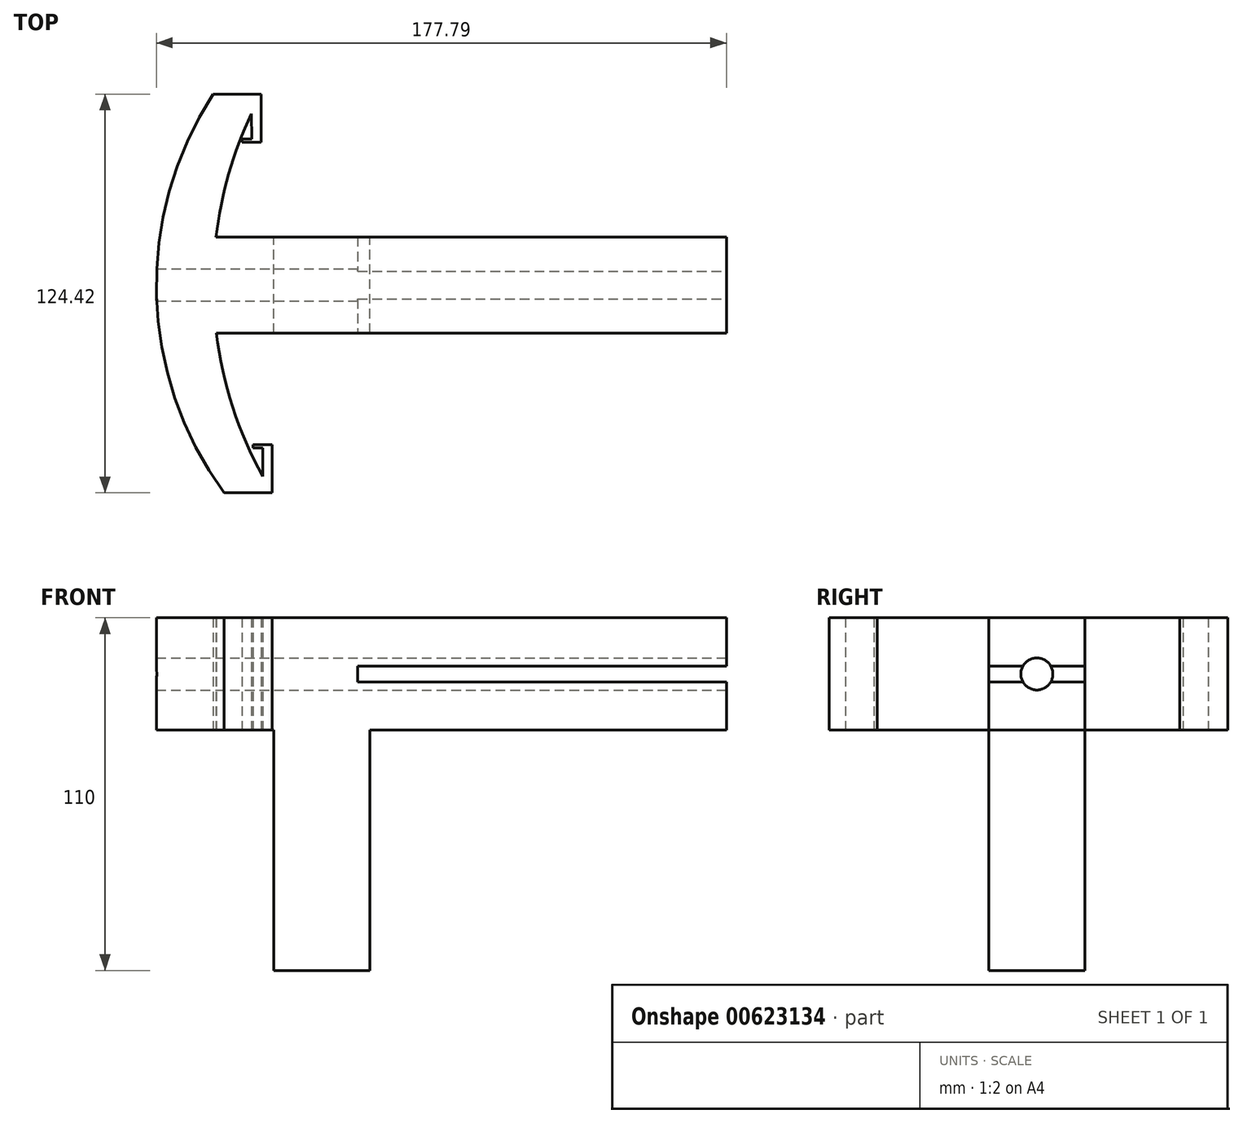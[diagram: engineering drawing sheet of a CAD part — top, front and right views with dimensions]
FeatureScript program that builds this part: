
annotation { "Feature Type Name" : "Feature", "Feature Type Description" : "" }
export const myFeature = defineFeature(function(context is Context, id is Id, definition is map)
    precondition{}
    {
        {
            var Q0;
            Q0=qCreatedBy(makeId("Top.planeOp"),FACE);
            var sketch = newSketch(context, id + "F0", { "sketchPlane" : qUnion([Q0])});
            skPoint(sketch, "E0", {"position": v(-80.73, 0) * mm});
            skArc(sketch, "E1", {"start": v(-62.98, 59.58) * mm, "mid": v(-80.7, -3.16) * mm, "end": v(-59.59, -64.84) * mm});
            skLineSegment(sketch, "E2", {"start": v(-62.98, 59.58) * mm, "end": v(-47.98, 59.58) * mm});
            skLineSegment(sketch, "E3", {"start": v(-59.59, -64.84) * mm, "end": v(-44.59, -64.84) * mm});
            skPoint(sketch, "E4", {"position": v(-62.98, 0) * mm});
            skArc(sketch, "E5", {"start": v(-51.1, 53.4) * mm, "mid": v(-58.16, 34.64) * mm, "end": v(-62.11, 15) * mm});
            skLineSegment(sketch, "E6.bottom", {"start": v(-62.94, -15) * mm, "end": v(97.06, -15) * mm});
            skLineSegment(sketch, "E6.top", {"start": v(-62.11, 15) * mm, "end": v(97.06, 15) * mm});
            skLineSegment(sketch, "E6.right", {"start": v(97.06, -15) * mm, "end": v(97.06, 15) * mm});
            skArc(sketch, "E7.trimOffspring", {"start": v(-62.04, -15) * mm, "mid": v(-56.94, -38.03) * mm, "end": v(-47.59, -59.68) * mm});
            skLineSegment(sketch, "E8", {"start": v(-44.59, -64.84) * mm, "end": v(-44.59, -49.84) * mm});
            skLineSegment(sketch, "E9", {"start": v(-44.59, -49.84) * mm, "end": v(-47.59, -49.84) * mm});
            skLineSegment(sketch, "E10", {"start": v(-47.59, -50.84) * mm, "end": v(-47.59, -59.68) * mm});
            skLineSegment(sketch, "E11", {"start": v(-47.59, -49.84) * mm, "end": v(-50.59, -49.84) * mm});
            skLineSegment(sketch, "E12", {"start": v(-50.59, -49.84) * mm, "end": v(-50.59, -50.84) * mm});
            skLineSegment(sketch, "E13", {"start": v(-50.59, -50.84) * mm, "end": v(-47.59, -50.84) * mm});
            skLineSegment(sketch, "E14", {"start": v(-62.11, 15) * mm, "end": v(-63.02, 15) * mm});
            skLineSegment(sketch, "E15", {"start": v(-47.98, 59.58) * mm, "end": v(-47.98, 44.58) * mm});
            skLineSegment(sketch, "E16", {"start": v(-47.98, 44.58) * mm, "end": v(-53.98, 44.58) * mm});
            skLineSegment(sketch, "E17", {"start": v(-53.98, 44.58) * mm, "end": v(-53.98, 45.58) * mm});
            skLineSegment(sketch, "E18", {"start": v(-51, 45.58) * mm, "end": v(-51.1, 53.4) * mm});
            skLineSegment(sketch, "E19", {"start": v(-53.98, 45.58) * mm, "end": v(-51, 45.58) * mm});
            skPoint(sketch, "E20.orphan", {"position": v(-50.98, 44.58) * mm});
            skSolve(sketch);
        }
        {
            var Q0;
            Q0 = qSketchRegion(id + "F0", true);
            var Q1;
            Q1=makeQuery(id+"F0.imprint","IMPRINT",FACE,{"disambiguationData":[TD([[makeQuery(id+"F0.imprint","IMPRINT",EDGE,{"derivedFrom":sQuery(id+"F0.wireOp",EDGE,"E1")}),1.0]])]});
            extrude(context, id + "F1", {"entities" : qUnion([Q0, Q1]), "depth" : 35 * mm, "offsetDistance" : 25 * mm});
        }
        {
            var Q0;
            Q0=makeQuery(id+"F1.opExtrude","SWEPT_FACE",FACE,{"disambiguationData":[OSD([sQuery(id+"F0.wireOp",EDGE,"E6.right")])]});
            var sketch = newSketch(context, id + "F2", { "sketchPlane" : qUnion([Q0])});
            skCircle(sketch, "E21", {"center": v(0, 17.5) * mm, "radius": 5 * mm});
            skPoint(sketch, "E22.orphan", {"position": v(0, 35) * mm});
            skPoint(sketch, "E23.trimOffspring.end.orphan", {"position": v(15, 17.5) * mm});
            skPoint(sketch, "E24.end.orphan", {"position": v(0, 0) * mm});
            skPoint(sketch, "E25.start.orphan", {"position": v(-15, 17.5) * mm});
            skSolve(sketch);
        }
        {
            var Q0;
            Q0=makeQuery(id+"F2.imprint","IMPRINT",FACE,{"disambiguationData":[TD([[makeQuery(id+"F2.imprint","IMPRINT",EDGE,{"derivedFrom":sQuery(id+"F2.wireOp",EDGE,"E21")}),1.0]])]});
            extrude(context, id + "F3", {"entities" : qUnion([Q0]), "operationType" : NewBodyOperationType.REMOVE, "oppositeDirection" : true, "depth" : 2000 * mm, "offsetDistance" : 25 * mm});
        }
        {
            var Q0;
            Q0=makeQuery(id+"F1.opExtrude","SWEPT_FACE",FACE,{"disambiguationData":[OSD([sQuery(id+"F0.wireOp",EDGE,"E6.bottom")])]});
            var sketch = newSketch(context, id + "F4", { "sketchPlane" : qUnion([Q0])});
            skLineSegment(sketch, "E26", {"start": v(-17.94, 17.5) * mm, "end": v(-17.94, 20) * mm});
            skLineSegment(sketch, "E27", {"start": v(-17.94, 17.5) * mm, "end": v(-17.94, 15) * mm});
            skLineSegment(sketch, "E28.bottom", {"start": v(-17.94, 20) * mm, "end": v(97.06, 20) * mm});
            skLineSegment(sketch, "E28.top", {"start": v(-17.94, 15.03) * mm, "end": v(97.06, 15.03) * mm});
            skLineSegment(sketch, "E28.right", {"start": v(97.06, 20) * mm, "end": v(97.06, 15.03) * mm});
            skPoint(sketch, "E29.start.orphan", {"position": v(97.06, 17.5) * mm});
            skSolve(sketch);
        }
        {
            var Q0;
            Q0 = qSketchRegion(id + "F4", true);
            extrude(context, id + "F5", {"entities" : qUnion([Q0]), "operationType" : NewBodyOperationType.REMOVE, "oppositeDirection" : true, "depth" : 70 * mm, "offsetDistance" : 25 * mm});
        }
        {
            var Q0;
            Q0=makeQuery(id+"F1.opExtrude","CAP_FACE",FACE,{"disambiguationData":[OSD([sQuery(id+"F0.wireOp",EDGE,"E1"),sQuery(id+"F0.wireOp",EDGE,"E2"),sQuery(id+"F0.wireOp",EDGE,"E3"),sQuery(id+"F0.wireOp",EDGE,"E5"),sQuery(id+"F0.wireOp",EDGE,"E6.bottom"),sQuery(id+"F0.wireOp",EDGE,"E6.top"),sQuery(id+"F0.wireOp",EDGE,"E6.right"),sQuery(id+"F0.wireOp",EDGE,"E7.trimOffspring"),sQuery(id+"F0.wireOp",EDGE,"E8"),sQuery(id+"F0.wireOp",EDGE,"E9"),sQuery(id+"F0.wireOp",EDGE,"E10"),sQuery(id+"F0.wireOp",EDGE,"E11"),sQuery(id+"F0.wireOp",EDGE,"E12"),sQuery(id+"F0.wireOp",EDGE,"E13"),sQuery(id+"F0.wireOp",EDGE,"E15"),sQuery(id+"F0.wireOp",EDGE,"E16"),sQuery(id+"F0.wireOp",EDGE,"E17"),sQuery(id+"F0.wireOp",EDGE,"E18"),sQuery(id+"F0.wireOp",EDGE,"E19")])],"isStart":true});
            var sketch = newSketch(context, id + "F6", { "sketchPlane" : qUnion([Q0])});
            skLineSegment(sketch, "E30.bottom", {"start": v(-44.11, 15) * mm, "end": v(-14.11, 15) * mm});
            skLineSegment(sketch, "E30.top", {"start": v(-44.11, -15) * mm, "end": v(-14.11, -15) * mm});
            skLineSegment(sketch, "E30.left", {"start": v(-44.11, 15) * mm, "end": v(-44.11, -15) * mm});
            skLineSegment(sketch, "E30.right", {"start": v(-14.11, 15) * mm, "end": v(-14.11, -15) * mm});
            skSolve(sketch);
        }
        {
            var Q0;
            Q0 = qSketchRegion(id + "F6", true);
            var Q1;
            Q1=makeQuery(id+"F6.imprint","IMPRINT",FACE,{"disambiguationData":[TD([[makeQuery(id+"F6.imprint","IMPRINT",EDGE,{"derivedFrom":sQuery(id+"F6.wireOp",EDGE,"E30.bottom")}),-1.0]])]});
            extrude(context, id + "F7", {"entities" : qUnion([Q0, Q1]), "operationType" : NewBodyOperationType.ADD, "depth" : 75 * mm, "offsetDistance" : 25 * mm});
        }
    });
